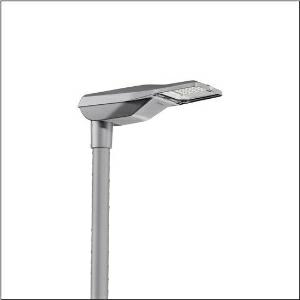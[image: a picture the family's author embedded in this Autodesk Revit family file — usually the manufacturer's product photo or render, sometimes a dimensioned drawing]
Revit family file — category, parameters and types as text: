
# Revit family: streetlight_sl_21_iq_micro___p0_5a_5xe1v31g08db_d973
name_source: partatom
category: Lighting Fixtures
units: mm (PartAtom-declared; Revit-internal decimal feet)

## family parameters
Cut with Voids When Loaded = No
Host = Face
Light Source = No
Part Type = Normal
Room Calculation Point = No
Round Connector Dimension = Use Diameter
Shared = No

## types (1)
- --- (1 x LED, 4660 lm, 36.4 W, 3000K)
    Apparent Load = 36 VA
    CIE Flux Codes = 37 73 96 100 100
    Color Rendering = 70
    Color Temperature = 3000K
    Default Elevation = 1800 mm
    Description = Streetlight SL 21 iQ micro, mast luminaire, primary light control with lens, of PMMA, primary optical cover: cover, of toughened safety glass, transparent, light distribution: P0.5a, light emission: direct distribution, primary light characteristic: asymmetric, installation type: post-top, side-entry, LED, High Power LED, rated luminous flux: 4.660lm, luminous efficacy: 128lm/W, light colour: 730, colour temperature: 3000K, control gear: iQ Street-Remote, control: pre-setting: linear dimming characteristic, Street-Remote, Auto-Match, Temp-Guard, Lumen-Switch, Night-Set, Smart-Wire, Light-Fading, Desk-Remote (wireless, voltage-free reading and setting of iQ features in the workshop via application-optimized NFC function/RFID function), optimised constant luminous flux control (CLO 2.0), mains connection: 220..240V, AC, 50/60Hz, start of lifetime: 36W, end of service life: 38W, reduction: 16W, luminaire housing, of diecast aluminium, powder-coated, SITECO metallic grey (DB 702S), corrosivity category C5 high according to DIN EN ISO 12944, please order mast flange separately, inclination adjustable: 0°, 5°, 10°, 15°, sealing non-destructively replaceable, multi-level sealing system, length: 528mm, width: 235mm, height: 110mm, mast flange for spigot size: 42mm (side-entry): 5XC10008XM4, 60/48mm (side-entry/post-top): 5XC10108XM2, 76/60mm (side-entry/post-top): 5XC10108XM1, protection rating (complete): IP66, insulation class (complete): insulation class II (safety insulation), certification: CE, ENEC, ENEC+, VDE, impact resistance: IK10, permissible operating ambient temperature for outdoor applications: -40..+50°C, standard-compliant lighting for roads and squares, packaging unit: 1 piece

Light Distribution: P0.5a
    Height = 110 mm
    Lamp = 1 x LED
    Lamp Light Flux = 4660 lm
    Lamp Power = 36.4 W
    Lamp count = 1
    Length = 528 mm
    Luminous efficacy = 128 lm/W
    Manufacturer = Siteco
    ModVariant = No
    Model = 5XE1V31G08DB
    Number of Poles = 1
    OnlyDefault = Yes
    Power Factor = 1
    Product Name = Streetlight SL 21 iQ micro | P0.5a
    Product group = mast luminaire | pylon top
    ProductGroupID = 6100
    Protection Class = Protection class II
    Protection Degree = IP 66
    RLX_Detail_Level = 1
    RLX_Emergency_Light_Flux = 0 lm
    RLX_Emergency_Type = 0
    RLX_Emergency_Type_DB = No
    RlxData = <blob elided: 98481 chars, md5=cc5b6689>
    Socket = socket
    Standby Power = 0 W
    System Light Flux = 4660 lm
    System Power = 36 W
    Type Comments = factory setting: luminous flux: 100 % | dim-lin: 254 | 715 mA
    Type Image = l_1006881.jpg
    URL = http://relux.com
    VarID = @adj_078107
    Voltage = 0 V
    Weight = 0.00 kg
    Width = 235 mm

## geometry (parser evidence)
native form markers: Blend x4, Sweep x9
no freeform markers — native parametric forms only
